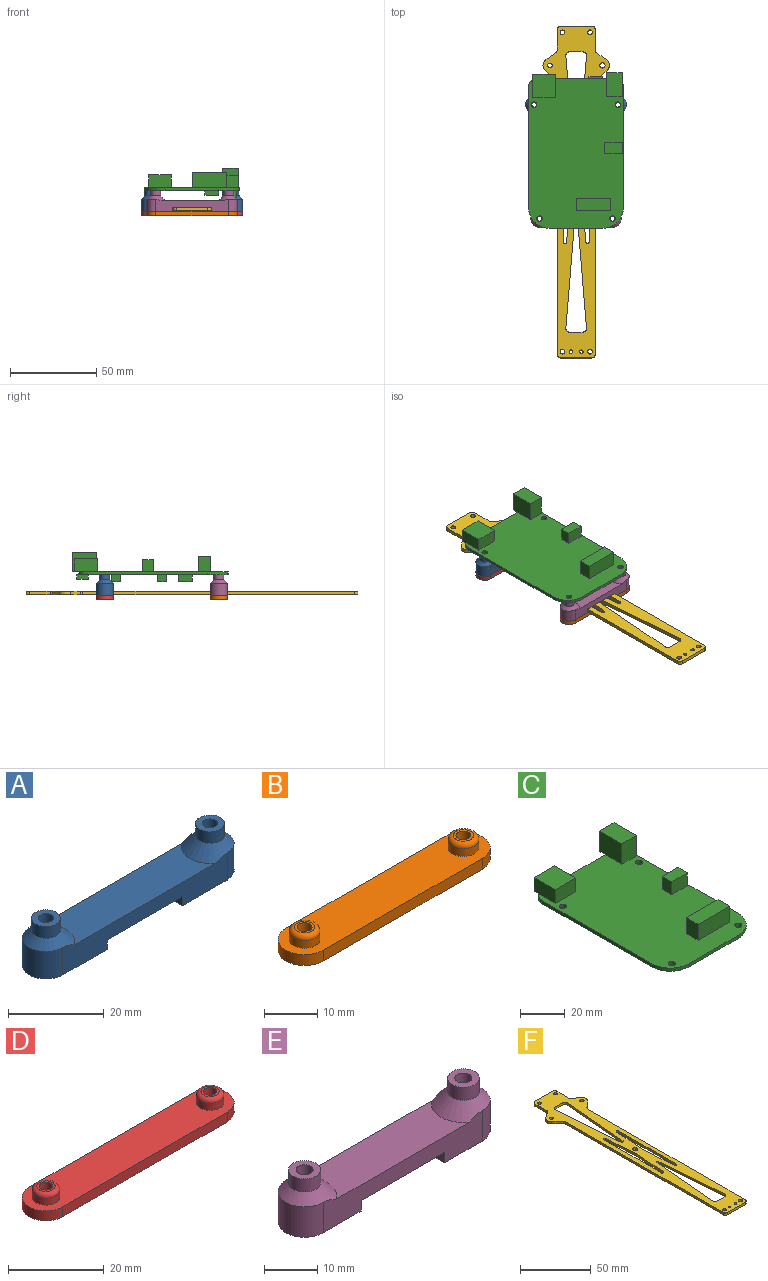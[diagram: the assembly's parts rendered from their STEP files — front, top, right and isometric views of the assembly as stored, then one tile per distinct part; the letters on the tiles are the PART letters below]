
ASSEMBLY  parts=6 mates=12
PART A: 22 faces, bbox 60.4x12x12 mm
  f0: cylinder r=1.6mm len=9mm, axis (0,0,1), area 90.5mm2, adj f5,f20
  f1: cylinder r=1.6mm len=9mm, axis (0,0,1), area 90.5mm2, adj f7,f19
  f2: plane 18.1x10mm, normal (0,0,-1), area 140.1mm2, adj f3,f9,f10,f16,f18
  f3: plane 48.4x7mm, normal (0,-1,0), area 241.5mm2, adj f2,f8,f10,f11,f12,f13,f14,f15
  f4: cylinder r=3mm len=6mm, axis (0,0,1), area 56.5mm2, adj f5,f14
  f5: plane 6x6mm, normal (0,0,1), area 20.2mm2, adj f0,f4
  f6: cylinder r=3mm len=6mm, axis (0,0,1), area 56.5mm2, adj f7,f13
  f7: plane 6x6mm, normal (0,0,1), area 20.2mm2, adj f1,f6
  f8: cylinder r=5mm len=10mm, axis (0,0,1), area 110mm2, adj f3,f9,f11,f14
  f9: plane 48.4x7mm, normal (0,1,0), area 241.5mm2, adj f2,f8,f10,f11,f12,f13,f14,f15
  f10: cylinder r=5mm len=10mm, axis (0,0,1), area 110mm2, adj f2,f3,f9,f13
  f11: plane 18.1x10mm, normal (0,0,-1), area 140.1mm2, adj f3,f8,f9,f15,f21
  f12: plane 41.77x10mm, normal (0,0,1), area 379.9mm2, adj f3,f9,f13,f14
  f13: cone r=6mm half-angle=45deg, axis (0,0,-1), area 89.2mm2, adj f3,f6,f9,f10,f12
  f14: cone r=6mm half-angle=45deg, axis (0,0,-1), area 89.2mm2, adj f3,f4,f8,f9,f12
  f15: plane 10x2.4mm, normal (1,0,0), area 24mm2, adj f3,f9,f11,f17
  f16: plane 10x2.4mm, normal (-1,0,0), area 24mm2, adj f2,f3,f9,f17
  f17: plane 22.2x10mm, normal (0,0,-1), area 222mm2, adj f3,f9,f15,f16
  f18: cylinder r=3.1mm len=6.2mm, axis (0,0,-1), area 58.4mm2, adj f2,f19
  f19: plane 6.2x6.2mm, normal (0,0,-1), area 22.1mm2, adj f1,f18
  f20: plane 6.2x6.2mm, normal (0,0,-1), area 22.1mm2, adj f0,f21
  f21: cylinder r=3.1mm len=6.2mm, axis (0,0,-1), area 58.4mm2, adj f11,f20
PART B: 14 faces, bbox 52.2x10x5.3 mm
  f0: plane 42.2x2.5mm, normal (0,1,0), area 105.5mm2, adj f1,f4,f6,f7
  f1: cylinder r=5mm len=10mm, axis (0,0,1), area 39.3mm2, adj f0,f2,f6,f7
  f2: plane 42.2x2.5mm, normal (0,-1,0), area 105.5mm2, adj f1,f4,f6,f7
  f3: cylinder r=1.4mm len=5.3mm, axis (0,0,1), area 46.6mm2, adj f6,f11
  f4: cylinder r=5mm len=10mm, axis (0,0,1), area 39.3mm2, adj f0,f2,f6,f7
  f5: cylinder r=1.4mm len=5.3mm, axis (0,0,1), area 46.6mm2, adj f6,f9
  f6: plane 52.2x10mm, normal (0,0,-1), area 488.2mm2, adj f0,f1,f2,f3,f4,f5
  f7: plane 52.2x10mm, normal (0,0,1), area 447.7mm2, adj f0,f1,f2,f4,f8,f10
  f8: cylinder r=2.9mm len=5.8mm, axis (0,0,-1), area 32.8mm2, adj f7,f13
  f9: plane 3.8x3.8mm, normal (0,0,1), area 5.2mm2, adj f5,f13
  f10: cylinder r=2.9mm len=5.8mm, axis (0,0,-1), area 32.8mm2, adj f7,f12
  f11: plane 3.8x3.8mm, normal (0,0,1), area 5.2mm2, adj f3,f12
  f12: torus R=1.9mm, axis (0,0,1), area 25mm2, adj f10,f11
  f13: torus R=1.9mm, axis (0,0,1), area 25mm2, adj f8,f9
PART C: 57 faces, bbox 55x89.9x17.1 mm
  f0: plane 86.4x55mm, normal (0,0,1), area 4205.2mm2, adj f1,f2,f3,f4,f5,f6,f7,f8
  f1: plane 45x1.7mm, normal (0,1,0), area 76.5mm2, adj f0,f2,f12,f13,f19,f25,f26
  f2: cylinder r=5mm len=5mm, axis (0,0,-1), area 13.4mm2, adj f0,f1,f3,f13,f19
  f3: plane 69.4x1.7mm, normal (-1,0,0), area 118mm2, adj f0,f2,f4,f13
  f4: cylinder r=12mm len=12mm, axis (0,0,-1), area 32mm2, adj f0,f3,f5,f13
  f5: plane 31x1.7mm, normal (0,-1,0), area 52.7mm2, adj f0,f4,f6,f13
  f6: cylinder r=12mm len=12mm, axis (0,0,-1), area 32mm2, adj f0,f5,f7,f13
  f7: plane 69.4x1.7mm, normal (1,0,0), area 118mm2, adj f0,f6,f12,f13
  f8: cylinder r=1.6mm len=3.2mm, axis (0,0,-1), area 17.1mm2, adj f0,f13
  f9: cylinder r=1.6mm len=3.2mm, axis (0,0,-1), area 17.1mm2, adj f0,f13
  f10: cylinder r=1.6mm len=3.2mm, axis (0,0,-1), area 17.1mm2, adj f0,f13
  f11: cylinder r=1.6mm len=3.2mm, axis (0,0,-1), area 17.1mm2, adj f0,f13
  f12: cylinder r=5mm len=5mm, axis (0,0,-1), area 13.4mm2, adj f0,f1,f7,f13,f25
  f13: plane 86.4x55mm, normal (0,0,-1), area 4490.5mm2, adj f1,f2,f3,f4,f5,f6,f7,f8
  f14: plane 13x7.5mm, normal (0,-1,0), area 97.5mm2, adj f0,f15,f17,f18
  f15: plane 13.5x7.5mm, normal (1,0,0), area 101.2mm2, adj f0,f14,f16,f18,f19
  f16: plane 13x7.5mm, normal (0,1,0), area 97.5mm2, adj f15,f17,f18,f19
  f17: plane 13.5x7.5mm, normal (-1,0,0), area 101.2mm2, adj f0,f14,f16,f18,f19
  f18: plane 13.5x13mm, normal (0,0,1), area 175.5mm2, adj f14,f15,f16,f17
  f19: plane 13x3.17mm, normal (0,0,-1), area 33mm2, adj f1,f2,f15,f16,f17
  f20: plane 11.2x9mm, normal (0,1,0), area 100.8mm2, adj f21,f23,f24,f25
  f21: plane 14x11.2mm, normal (-1,0,0), area 156.8mm2, adj f0,f20,f22,f24,f25
  f22: plane 11.2x9mm, normal (0,-1,0), area 100.8mm2, adj f0,f21,f23,f24
  f23: plane 14x11.2mm, normal (1,0,0), area 156.8mm2, adj f0,f20,f22,f24,f25
  f24: plane 14x9mm, normal (0,0,1), area 126mm2, adj f20,f21,f22,f23
  f25: plane 9x5.79mm, normal (0,0,-1), area 34.3mm2, adj f1,f12,f20,f21,f23
  f26: plane 8x1.2mm, normal (0,0,1), area 9.6mm2, adj f1,f27,f28,f30
  f27: plane 8x2.8mm, normal (0,1,0), area 22.4mm2, adj f26,f28,f30,f31
  f28: plane 6.75x2.8mm, normal (1,0,0), area 18.9mm2, adj f13,f26,f27,f29,f31
  f29: plane 8x2.8mm, normal (0,-1,0), area 22.4mm2, adj f13,f28,f30,f31
  f30: plane 6.75x2.8mm, normal (-1,0,0), area 18.9mm2, adj f13,f26,f27,f29,f31
  f31: plane 8x6.75mm, normal (0,0,-1), area 54mm2, adj f27,f28,f29,f30
  f32: plane 7.8x4mm, normal (0,-1,0), area 31.2mm2, adj f13,f33,f35,f36
  f33: plane 8x4mm, normal (-1,0,0), area 32mm2, adj f13,f32,f34,f36
  f34: plane 7.8x4mm, normal (0,1,0), area 31.2mm2, adj f13,f33,f35,f36
  f35: plane 8x4mm, normal (1,0,0), area 32mm2, adj f13,f32,f34,f36
  f36: plane 8x7.8mm, normal (0,0,-1), area 62.4mm2, adj f32,f33,f34,f35
  f37: plane 5x4.2mm, normal (0,-1,0), area 21mm2, adj f13,f38,f40,f41
  f38: plane 5x4.2mm, normal (-1,0,0), area 21mm2, adj f13,f37,f39,f41
  f39: plane 5x4.2mm, normal (0,1,0), area 21mm2, adj f13,f38,f40,f41
  f40: plane 5x4.2mm, normal (1,0,0), area 21mm2, adj f13,f37,f39,f41
  f41: plane 5x5mm, normal (0,0,-1), area 25mm2, adj f37,f38,f39,f40
  f42: plane 5x4.2mm, normal (0,-1,0), area 21mm2, adj f13,f43,f45,f46
  f43: plane 5x4.2mm, normal (-1,0,0), area 21mm2, adj f13,f42,f44,f46
  f44: plane 5x4.2mm, normal (0,1,0), area 21mm2, adj f13,f43,f45,f46
  f45: plane 5x4.2mm, normal (1,0,0), area 21mm2, adj f13,f42,f44,f46
  f46: plane 5x5mm, normal (0,0,-1), area 25mm2, adj f42,f43,f44,f45
  f47: plane 10x7mm, normal (0,-1,0), area 70mm2, adj f0,f48,f50,f51
  f48: plane 7x6mm, normal (1,0,0), area 42mm2, adj f0,f47,f49,f51
  f49: plane 10x7mm, normal (0,1,0), area 70mm2, adj f0,f48,f50,f51
  f50: plane 7x6mm, normal (-1,0,0), area 42mm2, adj f0,f47,f49,f51
  f51: plane 10x6mm, normal (0,0,1), area 60mm2, adj f47,f48,f49,f50
  f52: plane 20x8.7mm, normal (0,1,0), area 174mm2, adj f0,f53,f55,f56
  f53: plane 8.7x7.4mm, normal (-1,0,0), area 64.4mm2, adj f0,f52,f54,f56
  f54: plane 20x8.7mm, normal (0,-1,0), area 174mm2, adj f0,f53,f55,f56
  f55: plane 8.7x7.4mm, normal (1,0,0), area 64.4mm2, adj f0,f52,f54,f56
  f56: plane 20x7.4mm, normal (0,0,1), area 148mm2, adj f52,f53,f54,f55
PART D: 14 faces, bbox 58.4x10x5.3 mm
  f0: plane 48.4x2.5mm, normal (0,1,0), area 121mm2, adj f1,f4,f6,f7
  f1: cylinder r=5mm len=10mm, axis (0,0,1), area 39.3mm2, adj f0,f2,f6,f7
  f2: plane 48.4x2.5mm, normal (0,-1,0), area 121mm2, adj f1,f4,f6,f7
  f3: cylinder r=1.4mm len=5.3mm, axis (0,0,1), area 46.6mm2, adj f6,f11
  f4: cylinder r=5mm len=10mm, axis (0,0,1), area 39.3mm2, adj f0,f2,f6,f7
  f5: cylinder r=1.4mm len=5.3mm, axis (0,0,1), area 46.6mm2, adj f6,f9
  f6: plane 58.4x10mm, normal (0,0,-1), area 550.2mm2, adj f0,f1,f2,f3,f4,f5
  f7: plane 58.4x10mm, normal (0,0,1), area 509.7mm2, adj f0,f1,f2,f4,f8,f10
  f8: cylinder r=2.9mm len=5.8mm, axis (0,0,-1), area 32.8mm2, adj f7,f12
  f9: plane 3.8x3.8mm, normal (0,0,1), area 5.2mm2, adj f5,f12
  f10: cylinder r=2.9mm len=5.8mm, axis (0,0,-1), area 32.8mm2, adj f7,f13
  f11: plane 3.8x3.8mm, normal (0,0,1), area 5.2mm2, adj f3,f13
  f12: torus R=1.9mm, axis (0,0,1), area 25mm2, adj f8,f9
  f13: torus R=1.9mm, axis (0,0,1), area 25mm2, adj f10,f11
PART E: 22 faces, bbox 54.2x12x12 mm
  f0: cylinder r=1.6mm len=9mm, axis (0,0,1), area 90.5mm2, adj f7,f20
  f1: cylinder r=1.6mm len=9mm, axis (0,0,1), area 90.5mm2, adj f5,f19
  f2: plane 15x10mm, normal (0,0,-1), area 109.1mm2, adj f3,f9,f10,f14,f21
  f3: plane 42.2x7mm, normal (0,-1,0), area 204.3mm2, adj f2,f8,f10,f11,f12,f13,f14,f15
  f4: cylinder r=3mm len=6mm, axis (0,0,1), area 56.5mm2, adj f5,f16
  f5: plane 6x6mm, normal (0,0,1), area 20.2mm2, adj f1,f4
  f6: cylinder r=3mm len=6mm, axis (0,0,1), area 56.5mm2, adj f7,f17
  f7: plane 6x6mm, normal (0,0,1), area 20.2mm2, adj f0,f6
  f8: cylinder r=5mm len=10mm, axis (0,0,1), area 110mm2, adj f3,f9,f11,f16
  f9: plane 42.2x7mm, normal (0,1,0), area 204.3mm2, adj f2,f8,f10,f11,f12,f13,f14,f15
  f10: cylinder r=5mm len=10mm, axis (0,0,1), area 110mm2, adj f2,f3,f9,f17
  f11: plane 15x10mm, normal (0,0,-1), area 109.1mm2, adj f3,f8,f9,f13,f18
  f12: plane 35.57x10mm, normal (0,0,1), area 317.9mm2, adj f3,f9,f16,f17
  f13: plane 10x2.4mm, normal (1,0,0), area 24mm2, adj f3,f9,f11,f15
  f14: plane 10x2.4mm, normal (-1,0,0), area 24mm2, adj f2,f3,f9,f15
  f15: plane 22.2x10mm, normal (0,0,-1), area 222mm2, adj f3,f9,f13,f14
  f16: cone r=6mm half-angle=45deg, axis (0,0,-1), area 89.2mm2, adj f3,f4,f8,f9,f12
  f17: cone r=6mm half-angle=45deg, axis (0,0,-1), area 89.2mm2, adj f3,f6,f9,f10,f12
  f18: cylinder r=3.1mm len=6.2mm, axis (0,0,-1), area 58.4mm2, adj f11,f19
  f19: plane 6.2x6.2mm, normal (0,0,-1), area 22.1mm2, adj f1,f18
  f20: plane 6.2x6.2mm, normal (0,0,-1), area 22.1mm2, adj f0,f21
  f21: cylinder r=3.1mm len=6.2mm, axis (0,0,-1), area 58.4mm2, adj f2,f20
PART F: 53 faces, bbox 38.4x192x2 mm
  f0: cylinder r=1mm len=2mm, axis (0,0,-1), area 6.1mm2, adj f1,f50,f51,f52
  f1: plane 60.88x4.99mm, normal (1,0.08,0), area 122.2mm2, adj f0,f2,f51,f52
  f2: cylinder r=2mm len=2.16mm, axis (0,0,-1), area 6.6mm2, adj f1,f3,f51,f52
  f3: plane 8x2mm, normal (0,-1,0), area 16mm2, adj f2,f4,f51,f52
  f4: cylinder r=2mm len=2.16mm, axis (0,0,-1), area 6.6mm2, adj f3,f50,f51,f52
  f5: plane 8x2mm, normal (0,1,0), area 16mm2, adj f6,f37,f51,f52
  f6: cylinder r=2mm len=2.16mm, axis (0,0,-1), area 6.6mm2, adj f5,f7,f51,f52
  f7: plane 60.88x4.99mm, normal (1,-0.08,0), area 122.2mm2, adj f6,f8,f51,f52
  f8: cylinder r=1mm len=2mm, axis (0,0,-1), area 6.1mm2, adj f7,f9,f51,f52
  f9: plane 60.88x4.99mm, normal (-1,-0.08,0), area 122.2mm2, adj f8,f37,f51,f52
  f10: plane 157.11x2mm, normal (1,0,0), area 314.2mm2, adj f11,f38,f51,f52
  f11: cylinder r=2mm len=2mm, axis (0,0,-1), area 3.3mm2, adj f10,f12,f51,f52
  f12: plane 6.23x5.64mm, normal (0.67,-0.74,0), area 16.8mm2, adj f11,f13,f51,f52
  f13: cylinder r=4mm len=6.25mm, axis (0,0,-1), area 14.4mm2, adj f12,f14,f51,f52
  f14: plane 5.63x3.92mm, normal (0.57,0.82,0), area 13.7mm2, adj f13,f15,f51,f52
  f15: cylinder r=2mm len=2mm, axis (0,0,-1), area 3.8mm2, adj f14,f16,f51,f52
  f16: plane 11.96x2mm, normal (1,0,0), area 23.9mm2, adj f15,f17,f51,f52
  f17: cylinder r=2mm len=2mm, axis (0,0,-1), area 6.3mm2, adj f16,f18,f51,f52
  f18: plane 18x2mm, normal (0,1,0), area 36mm2, adj f17,f19,f51,f52
  f19: cylinder r=2mm len=2mm, axis (0,0,-1), area 6.3mm2, adj f18,f20,f51,f52
  f20: plane 11.96x2mm, normal (-1,0,0), area 23.9mm2, adj f19,f21,f51,f52
  f21: cylinder r=2mm len=2mm, axis (0,0,-1), area 3.8mm2, adj f20,f22,f51,f52
  f22: plane 5.63x3.92mm, normal (-0.57,0.82,0), area 13.7mm2, adj f21,f23,f51,f52
  f23: cylinder r=4mm len=6.25mm, axis (0,0,-1), area 14.4mm2, adj f22,f24,f51,f52
  f24: plane 6.23x5.64mm, normal (-0.67,-0.74,0), area 16.8mm2, adj f23,f25,f51,f52
  f25: cylinder r=2mm len=2mm, axis (0,0,-1), area 3.3mm2, adj f24,f26,f51,f52
  f26: plane 157.11x2mm, normal (-1,0,0), area 314.2mm2, adj f25,f27,f51,f52
  f27: cylinder r=2mm len=2mm, axis (0,0,-1), area 6.3mm2, adj f26,f28,f51,f52
  f28: plane 18x2mm, normal (0,-1,0), area 36mm2, adj f27,f38,f51,f52
  f29: plane 57.5x2mm, normal (1,0,0), area 115mm2, adj f30,f39,f51,f52
  f30: cylinder r=1mm len=2mm, axis (0,0,-1), area 6.3mm2, adj f29,f31,f51,f52
  f31: plane 28.75x2mm, normal (-1,-0.07,0), area 57.6mm2, adj f30,f32,f51,f52
  f32: plane 28.75x2mm, normal (-1,0.07,0), area 57.6mm2, adj f31,f39,f51,f52
  f33: plane 57.5x2mm, normal (-1,0,0), area 115mm2, adj f34,f49,f51,f52
  f34: cylinder r=1mm len=2mm, axis (0,0,-1), area 6.3mm2, adj f33,f35,f51,f52
  f35: plane 28.75x2mm, normal (1,0.07,0), area 57.6mm2, adj f34,f36,f51,f52
  f36: plane 28.75x2mm, normal (1,-0.07,0), area 57.6mm2, adj f35,f49,f51,f52
  f37: cylinder r=2mm len=2.16mm, axis (0,0,-1), area 6.6mm2, adj f5,f9,f51,f52
  f38: cylinder r=2mm len=2mm, axis (0,0,-1), area 6.3mm2, adj f10,f28,f51,f52
  f39: cylinder r=1mm len=2mm, axis (0,0,-1), area 6.3mm2, adj f29,f32,f51,f52
  f40: cylinder r=1.5mm len=3mm, axis (0,0,-1), area 18.8mm2, adj f51,f52
  f41: cylinder r=1.35mm len=2.7mm, axis (0,0,-1), area 17mm2, adj f51,f52
  f42: cylinder r=1.35mm len=2.7mm, axis (0,0,-1), area 17mm2, adj f51,f52
  f43: cylinder r=1.35mm len=2.7mm, axis (0,0,-1), area 17mm2, adj f51,f52
  f44: cylinder r=1.35mm len=2.7mm, axis (0,0,-1), area 17mm2, adj f51,f52
  f45: cylinder r=1mm len=2mm, axis (0,0,-1), area 12.6mm2, adj f51,f52
  f46: cylinder r=1.75mm len=3.5mm, axis (0,0,-1), area 22mm2, adj f51,f52
  f47: cylinder r=1mm len=2mm, axis (0,0,-1), area 12.6mm2, adj f51,f52
  f48: cylinder r=1.35mm len=2.7mm, axis (0,0,-1), area 17mm2, adj f51,f52
  f49: cylinder r=1mm len=2mm, axis (0,0,-1), area 6.3mm2, adj f33,f36,f51,f52
  f50: plane 60.88x4.99mm, normal (-1,0.08,0), area 122.2mm2, adj f0,f4,f51,f52
  f51: plane 192x38.4mm, normal (0,0,1), area 3084.3mm2, adj f0,f1,f2,f3,f4,f5,f6,f7
  f52: plane 192x38.4mm, normal (0,0,-1), area 3084.3mm2, adj f0,f1,f2,f3,f4,f5,f6,f7
PLACE A t=(-12.2,-17.37,19.33)mm
PLACE B t=(-12.2,-17.37,19.33)mm
PLACE C t=(-12.2,-17.37,19.33)mm
PLACE D t=(-12.2,-17.37,19.33)mm
PLACE E t=(-12.2,-17.37,19.33)mm
PLACE F t=(-12.1,-39.63,7.73)mm
MATE cylindrical D.f4 <-> A.f0  axis (0,0,-1) through (-36.4,10.83,7.33)mm
MATE cylindrical B.f1 <-> E.f0  axis (0,0,1) through (8.9,-55.07,4.83)mm
MATE cylindrical D.f1 <-> A.f1  axis (0,0,1) through (12,10.83,4.83)mm
MATE cylindrical E.f0 <-> C.f10  axis (0,0,1) through (8.9,-55.07,19.33)mm
MATE planar F.f10 <-> E.f14  axis (1,0,0) through (-1.1,-55.07,8.73)mm
MATE cylindrical E.f1 <-> C.f11  axis (0,0,1) through (-33.3,-55.07,19.33)mm
MATE planar F.f51 <-> E.f15  axis (0,0,1) through (-18.1,-118.47,9.73)mm
MATE cylindrical B.f4 <-> E.f1  axis (0,0,1) through (-33.3,-55.07,7.33)mm
MATE planar B.f7 <-> E.f2  axis (0,0,1) through (-12.2,-55.07,7.33)mm
MATE planar D.f7 <-> A.f2  axis (0,0,1) through (-12.2,10.83,7.33)mm
MATE cylindrical A.f1 <-> C.f9  axis (0,0,1) through (12,10.83,19.33)mm
MATE cylindrical A.f0 <-> C.f8  axis (0,0,1) through (-36.4,10.83,19.33)mm
